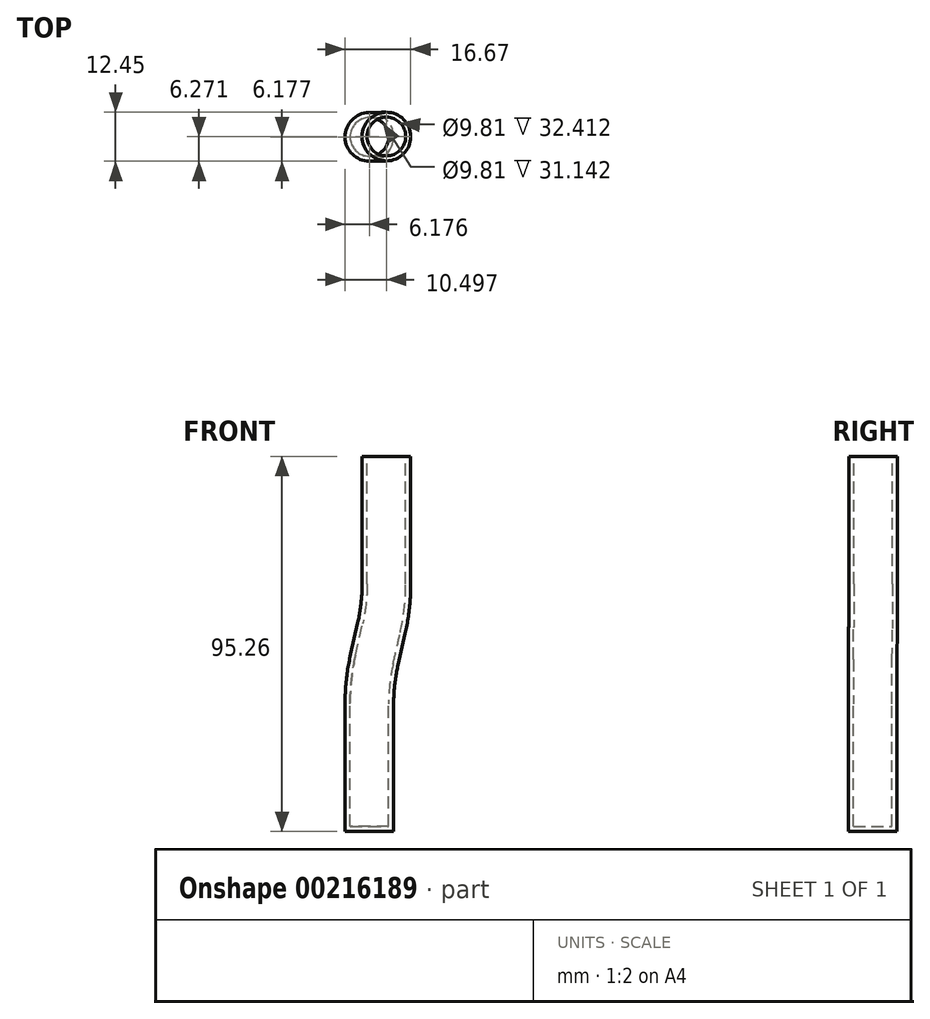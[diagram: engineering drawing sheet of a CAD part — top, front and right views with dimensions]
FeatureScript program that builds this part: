
annotation { "Feature Type Name" : "Feature", "Feature Type Description" : "" }
export const myFeature = defineFeature(function(context is Context, id is Id, definition is map)
    precondition{}
    {
        {
            var Q0;
            Q0=qCreatedBy(makeId("Top.planeOp"),FACE);
            var sketch = newSketch(context, id + "F0", { "sketchPlane" : qUnion([Q0])});
            skLineSegment(sketch, "E0", {"start": v(0, 0) * mm, "end": v(-185.8, 0) * mm});
            skLineSegment(sketch, "E1", {"start": v(-185.8, 0) * mm, "end": v(-185.8, 258.16) * mm});
            skLineSegment(sketch, "E2", {"start": v(-185.8, 258.16) * mm, "end": v(-160.4, 258.16) * mm});
            skLineSegment(sketch, "E3", {"start": v(0, 0) * mm, "end": v(-190.11, 0) * mm});
            skLineSegment(sketch, "E4", {"start": v(-190.11, 0) * mm, "end": v(-190.11, 258.07) * mm});
            skLineSegment(sketch, "E5", {"start": v(-190.11, 258.07) * mm, "end": v(-215.51, 258.07) * mm});
            skSolve(sketch);
        }
        {
            var Q0;
            Q0=sQuery(id+"F0.wireOp",EDGE,"E2");
            cPlane(context, id + "F1", {"entities" : qUnion([Q0]), "cplaneType" : CPlaneType.LINE_ANGLE, "offset" : 25.4 * mm, "angle" : 0 * degree, "width" : 152.4 * mm, "height" : 152.4 * mm});
        }
        {
            var Q0;
            Q0=qCreatedBy(id+"F1.planeOp",FACE);
            var sketch = newSketch(context, id + "F2", { "sketchPlane" : qUnion([Q0])});
            skLineSegment(sketch, "E6", {"start": v(185.8, 0) * mm, "end": v(185.8, -333.9) * mm});
            skLineSegment(sketch, "E7", {"start": v(185.8, -333.9) * mm, "end": v(160.4, -333.9) * mm});
            skSolve(sketch);
        }
        {
            var Q0;
            Q0=sQuery(id+"F0.wireOp",EDGE,"E5");
            cPlane(context, id + "F3", {"entities" : qUnion([Q0]), "cplaneType" : CPlaneType.LINE_ANGLE, "offset" : 25.4 * mm, "angle" : 0 * degree, "width" : 152.4 * mm, "height" : 152.4 * mm});
        }
        {
            var Q0;
            Q0=qCreatedBy(id+"F3.planeOp",FACE);
            var sketch = newSketch(context, id + "F4", { "sketchPlane" : qUnion([Q0])});
            skLineSegment(sketch, "E8", {"start": v(-190.11, 0) * mm, "end": v(-190.11, -429.15) * mm});
            skLineSegment(sketch, "E9", {"start": v(-190.11, -429.15) * mm, "end": v(-164.71, -429.15) * mm});
            skSolve(sketch);
        }
        {
            var Q0;
            Q0=sQuery(id+"F2.wireOp",EDGE,"E7");
            cPlane(context, id + "F5", {"entities" : qUnion([Q0]), "cplaneType" : CPlaneType.LINE_ANGLE, "offset" : 25.4 * mm, "angle" : 90 * degree, "width" : 152.4 * mm, "height" : 152.4 * mm});
        }
        {
            var Q0;
            Q0=qCreatedBy(id+"F5.planeOp",FACE);
            var sketch = newSketch(context, id + "F6", { "sketchPlane" : qUnion([Q0])});
            skCircle(sketch, "E10", {"center": v(-185.8, 258.16) * mm, "radius": 6.18 * mm});
            skSolve(sketch);
        }
        {
            var Q0;
            Q0=sQuery(id+"F2.wireOp",EDGE,"E7");
            cPlane(context, id + "F7", {"entities" : qUnion([Q0]), "cplaneType" : CPlaneType.LINE_ANGLE, "offset" : 25.4 * mm, "angle" : 0 * degree, "width" : 152.4 * mm, "height" : 152.4 * mm});
        }
        {
            var Q0;
            Q0=qCreatedBy(id+"F7.planeOp",FACE);
            var sketch = newSketch(context, id + "F8", { "sketchPlane" : qUnion([Q0])});
            skLineSegment(sketch, "E11", {"start": v(185.8, -333.9) * mm, "end": v(185.8, -384.7) * mm});
            skLineSegment(sketch, "E12", {"start": v(185.8, -333.9) * mm, "end": v(185.8, -372) * mm});
            skSolve(sketch);
        }
        {
            var Q0;
            Q0=sQuery(id+"F4.wireOp",EDGE,"E9");
            cPlane(context, id + "F9", {"entities" : qUnion([Q0]), "cplaneType" : CPlaneType.LINE_ANGLE, "offset" : 25.4 * mm, "angle" : 90 * degree, "width" : 152.4 * mm, "height" : 152.4 * mm});
        }
        {
            var Q0;
            Q0=qCreatedBy(id+"F9.planeOp",FACE);
            var sketch = newSketch(context, id + "F10", { "sketchPlane" : qUnion([Q0])});
            skCircle(sketch, "E13", {"center": v(-190.11, 258.07) * mm, "radius": 6.18 * mm});
            skSolve(sketch);
        }
        {
            var Q0;
            Q0=sQuery(id+"F4.wireOp",EDGE,"E9");
            cPlane(context, id + "F11", {"entities" : qUnion([Q0]), "cplaneType" : CPlaneType.LINE_ANGLE, "offset" : 25.4 * mm, "angle" : 0 * degree, "width" : 152.4 * mm, "height" : 152.4 * mm});
        }
        {
            var Q0;
            Q0=qCreatedBy(id+"F11.planeOp",FACE);
            var sketch = newSketch(context, id + "F12", { "sketchPlane" : qUnion([Q0])});
            skLineSegment(sketch, "E14", {"start": v(190.11, -429.15) * mm, "end": v(190.11, -378.35) * mm});
            skLineSegment(sketch, "E15", {"start": v(190.11, -429.15) * mm, "end": v(190.11, -391.05) * mm});
            skSolve(sketch);
        }
        {
            var Q0;
            Q0=sQuery(id+"F12.wireOp",VERTEX,"E15.end");
            var Q1;
            Q1=sQuery(id+"F8.wireOp",VERTEX,"E12.end");
            var Q2;
            Q2=sQuery(id+"F8.wireOp",VERTEX,"E11.start");
            cPlane(context, id + "F13", {"entities" : qUnion([Q0, Q1, Q2]), "cplaneType" : CPlaneType.THREE_POINT, "offset" : 25.4 * mm, "width" : 152.4 * mm, "height" : 152.4 * mm});
        }
        {
            var Q0;
            Q0=qCreatedBy(id+"F13.planeOp",FACE);
            var sketch = newSketch(context, id + "F14", { "sketchPlane" : qUnion([Q0])});
            skLineSegment(sketch, "E16", {"start": v(181.4, -377.54) * mm, "end": v(184.46, -391.05) * mm});
            skLineSegment(sketch, "E17", {"start": v(180.14, -366.3) * mm, "end": v(180.14, -333.9) * mm});
            skPoint(sketch, "E18.visualSharp", {"position": v(180.14, -372) * mm});
            skArc(sketch, "E18.filletArc", {"start": v(180.14, -366.3) * mm, "mid": v(180.45, -371.96) * mm, "end": v(181.4, -377.54) * mm});
            skSolve(sketch);
        }
        {
            var Q0;
            Q0=sQuery(id+"F14.wireOp",VERTEX,"E16.start");
            var Q1;
            Q1=sQuery(id+"F14.wireOp",VERTEX,"E16.end");
            var Q2;
            Q2=sQuery(id+"F12.wireOp",VERTEX,"E15.start");
            cPlane(context, id + "F15", {"entities" : qUnion([Q0, Q1, Q2]), "cplaneType" : CPlaneType.THREE_POINT, "offset" : 25.4 * mm, "width" : 152.4 * mm, "height" : 152.4 * mm});
        }
        {
            var Q0;
            Q0=qCreatedBy(id+"F15.planeOp",FACE);
            var sketch = newSketch(context, id + "F16", { "sketchPlane" : qUnion([Q0])});
            skLineSegment(sketch, "E19", {"start": v(184.46, -429.15) * mm, "end": v(184.46, -396.74) * mm});
            skLineSegment(sketch, "E20", {"start": v(183.2, -385.5) * mm, "end": v(181.4, -377.54) * mm});
            skPoint(sketch, "E21.visualSharp", {"position": v(184.46, -391.05) * mm});
            skArc(sketch, "E21.filletArc", {"start": v(184.46, -396.74) * mm, "mid": v(184.14, -391.08) * mm, "end": v(183.2, -385.5) * mm});
            skSolve(sketch);
        }
        {
            var Q0;
            Q0=makeQuery(id+"F10.imprint","IMPRINT",FACE,{"disambiguationData":[TD([[makeQuery(id+"F10.imprint","IMPRINT",EDGE,{"derivedFrom":sQuery(id+"F10.wireOp",EDGE,"E13")}),1.0]])]});
            var Q1;
            Q1=sQuery(id+"F16.wireOp",EDGE,"E19");
            var Q2;
            Q2=sQuery(id+"F16.wireOp",EDGE,"E21.filletArc");
            var Q3;
            Q3=sQuery(id+"F16.wireOp",EDGE,"E20");
            var Q4;
            Q4=sQuery(id+"F14.wireOp",EDGE,"E18.filletArc");
            var Q5;
            Q5=sQuery(id+"F14.wireOp",EDGE,"E17");
            sweep(context, id + "F17", {"profiles" : qUnion([Q0]), "path" : qUnion([Q1, Q2, Q3, Q4, Q5])});
        }
        {
            var Q0;
            Q0=makeQuery(id+"F17.opSweep","CAP_FACE",FACE,{"disambiguationData":[OSD([sQuery(id+"F10.wireOp",EDGE,"E13"),sQuery(id+"F14.wireOp",VERTEX,"E17.end")])],"isStart":false});
            shell(context, id + "F18", {"entities" : qUnion([Q0]), "thickness" : 1.27 * mm});
        }
    });
